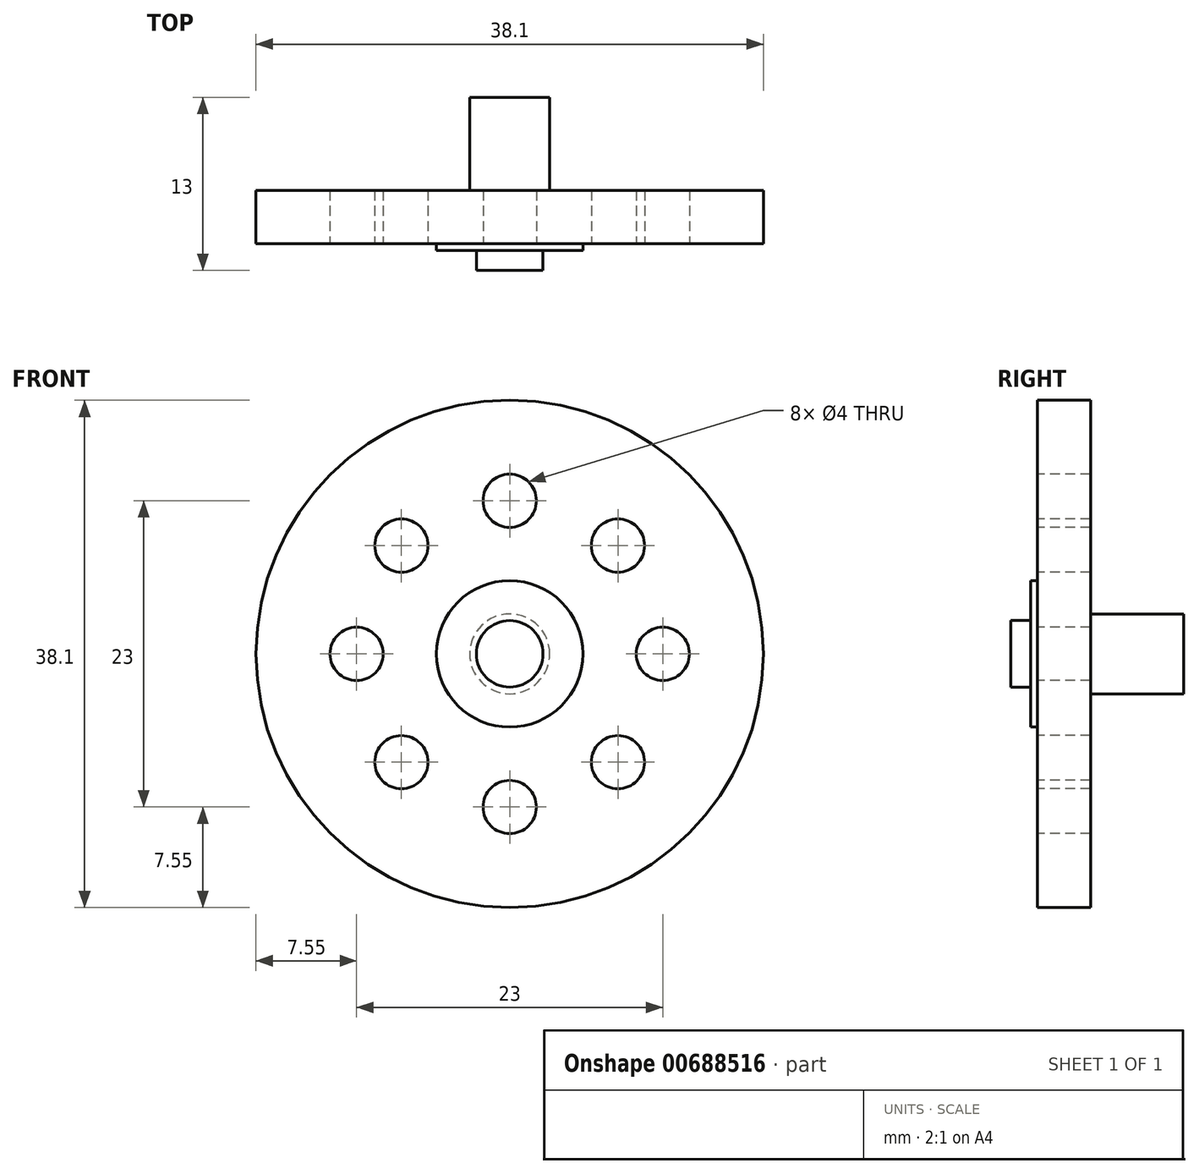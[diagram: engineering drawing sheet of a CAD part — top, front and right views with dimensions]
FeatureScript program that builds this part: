
annotation { "Feature Type Name" : "Feature", "Feature Type Description" : "" }
export const myFeature = defineFeature(function(context is Context, id is Id, definition is map)
    precondition{}
    {
        {
            var Q0;
            Q0=qCreatedBy(makeId("Front.planeOp"),FACE);
            var sketch = newSketch(context, id + "F0", { "sketchPlane" : qUnion([Q0])});
            skCircle(sketch, "E0", {"center": v(0, 0) * mm, "radius": 19.05 * mm});
            skSolve(sketch);
        }
        {
            var Q0;
            Q0 = qSketchRegion(id + "F0", true);
            extrude(context, id + "F1", {"entities" : qUnion([Q0]), "depth" : 4 * mm, "offsetDistance" : 25 * mm});
        }
        {
            var Q0;
            Q0=makeQuery(id+"F1.opExtrude","CAP_FACE",FACE,{"disambiguationData":[OSD([sQuery(id+"F0.wireOp",EDGE,"E0")])],"isStart":false});
            var sketch = newSketch(context, id + "F2", { "sketchPlane" : qUnion([Q0])});
            skCircle(sketch, "E1", {"center": v(0, 0) * mm, "radius": 5.5 * mm});
            skCircle(sketch, "E2", {"center": v(0, 0) * mm, "radius": 2.5 * mm});
            skSolve(sketch);
        }
        {
            var Q0;
            Q0=makeQuery(id+"F2.imprint","IMPRINT",FACE,{"disambiguationData":[TD([[makeQuery(id+"F2.imprint","IMPRINT",EDGE,{"derivedFrom":sQuery(id+"F2.wireOp",EDGE,"E1")}),1.0]])]});
            extrude(context, id + "F3", {"entities" : qUnion([Q0]), "operationType" : NewBodyOperationType.ADD, "depth" : .5 * mm, "offsetDistance" : 25 * mm});
        }
        {
            var Q0;
            Q0=makeQuery(id+"F3.boolean.opBoolean","SPLIT",FACE,{"disambiguationData":[TD([makeQuery(id+"F3.opExtrude","SWEPT_FACE",FACE,{"disambiguationData":[OSD([sQuery(id+"F2.wireOp",EDGE,"E2")])]})])],"derivedFrom":makeQuery(id+"F1.opExtrude","CAP_FACE",FACE,{"disambiguationData":[OSD([sQuery(id+"F0.wireOp",EDGE,"E0")])],"isStart":false})});
            extrude(context, id + "F4", {"entities" : qUnion([Q0]), "operationType" : NewBodyOperationType.ADD, "depth" : 1 * mm, "offsetDistance" : 25 * mm});
        }
        {
            var Q0;
            Q0=makeQuery(id+"F4.opExtrude","CAP_FACE",FACE,{"disambiguationData":[OSD([sQuery(id+"F0.wireOp",EDGE,"E0")])],"isStart":false});
            extrude(context, id + "F5", {"entities" : qUnion([Q0]), "operationType" : NewBodyOperationType.ADD, "depth" : 1 * mm, "offsetDistance" : 25 * mm});
        }
        {
            var Q0;
            Q0=makeQuery(id+"F1.opExtrude","CAP_FACE",FACE,{"disambiguationData":[OSD([sQuery(id+"F0.wireOp",EDGE,"E0")])],"isStart":true});
            var sketch = newSketch(context, id + "F6", { "sketchPlane" : qUnion([Q0])});
            skCircle(sketch, "E3", {"center": v(0, 0) * mm, "radius": 3 * mm});
            skSolve(sketch);
        }
        {
            var Q0;
            Q0 = qSketchRegion(id + "F6", true);
            extrude(context, id + "F7", {"entities" : qUnion([Q0]), "operationType" : NewBodyOperationType.ADD, "depth" : 7 * mm, "offsetDistance" : 25 * mm});
        }
        {
            var Q0;
            {var subQ0=sQuery(id+"F0.wireOp",EDGE,"E0");Q0=makeQuery(id+"F3.boolean.opBoolean","SPLIT",FACE,{"disambiguationData":[TD([makeQuery(id+"F1.opExtrude","SWEPT_FACE",FACE,{"disambiguationData":[OSD([subQ0])]})])],"derivedFrom":makeQuery(id+"F1.opExtrude","CAP_FACE",FACE,{"disambiguationData":[OSD([subQ0])],"isStart":false})});}
            var sketch = newSketch(context, id + "F8", { "sketchPlane" : qUnion([Q0])});
            skCircle(sketch, "E4", {"center": v(0, 11.5) * mm, "radius": 2 * mm});
            skCircle(sketch, "E5.1.0", {"center": v(-8.13, 8.13) * mm, "radius": 2 * mm});
            skCircle(sketch, "E5.2.0", {"center": v(-11.5, 0) * mm, "radius": 2 * mm});
            skCircle(sketch, "E5.3.0", {"center": v(-8.13, -8.13) * mm, "radius": 2 * mm});
            skCircle(sketch, "E5.4.0", {"center": v(0, -11.5) * mm, "radius": 2 * mm});
            skCircle(sketch, "E5.5.0", {"center": v(8.13, -8.13) * mm, "radius": 2 * mm});
            skCircle(sketch, "E5.6.0", {"center": v(11.5, 0) * mm, "radius": 2 * mm});
            skCircle(sketch, "E5.7.0", {"center": v(8.13, 8.13) * mm, "radius": 2 * mm});
            skPoint(sketch, "E5.center", {"position": v(0, 0) * mm});
            skSolve(sketch);
        }
        {
            var Q0;
            Q0 = qSketchRegion(id + "F8", true);
            extrude(context, id + "F9", {"entities" : qUnion([Q0]), "operationType" : NewBodyOperationType.REMOVE, "oppositeDirection" : true, "depth" : 25 * mm, "offsetDistance" : 25 * mm});
        }
    });
